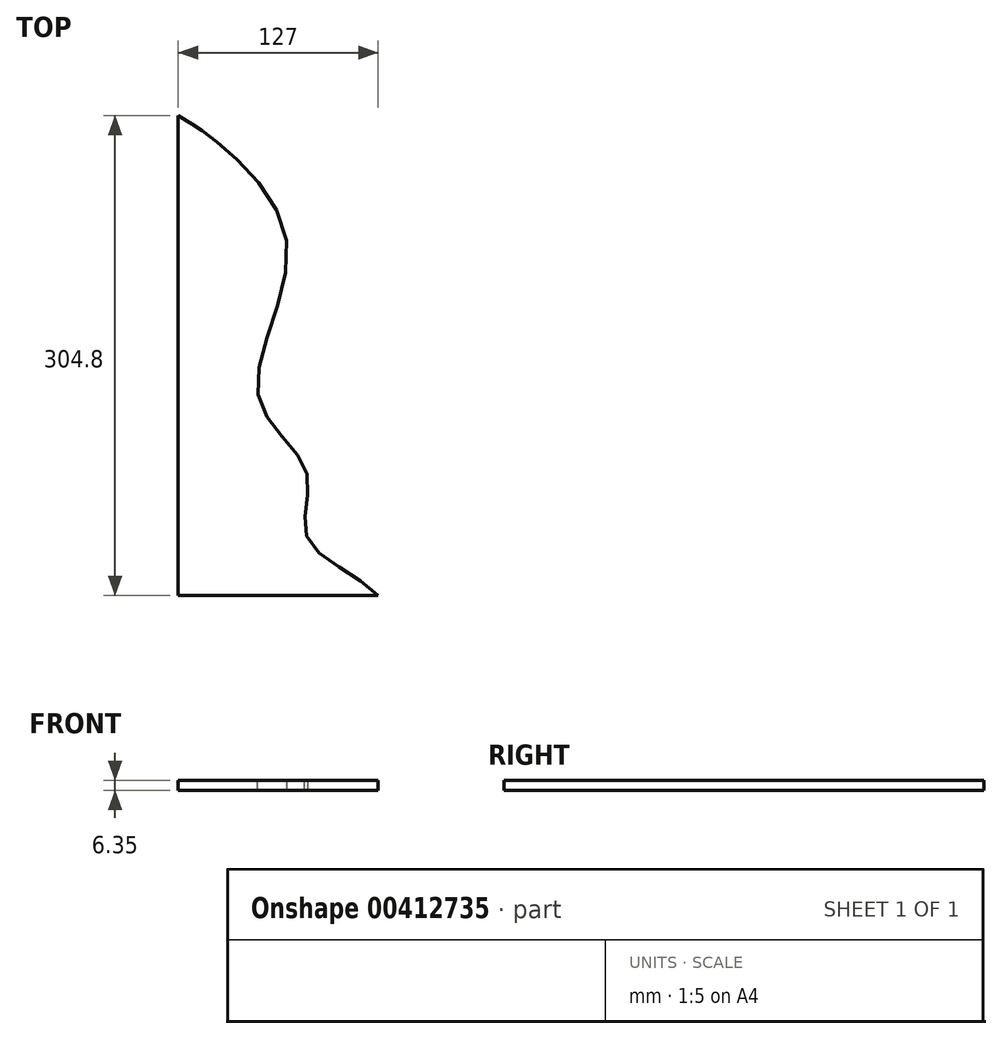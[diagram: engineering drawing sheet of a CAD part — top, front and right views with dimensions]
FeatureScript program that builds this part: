
annotation { "Feature Type Name" : "Feature", "Feature Type Description" : "" }
export const myFeature = defineFeature(function(context is Context, id is Id, definition is map)
    precondition{}
    {
        {
            var Q0;
            Q0=qCreatedBy(makeId("Top.planeOp"),FACE);
            var sketch = newSketch(context, id + "F0", { "sketchPlane" : qUnion([Q0])});
            skLineSegment(sketch, "E0", {"start": v(0, 0) * mm, "end": v(127, 0) * mm});
            skLineSegment(sketch, "E1", {"start": v(0, 0) * mm, "end": v(0, 304.8) * mm});
            skLineSegment(sketch, "E2", {"start": v(0, 127) * mm, "end": v(50.8, 127) * mm, "construction": true});
            skLineSegment(sketch, "E3", {"start": v(0, 293.37) * mm, "end": v(17.78, 293.37) * mm, "construction": true});
            skLineSegment(sketch, "E4", {"start": v(0, 226.06) * mm, "end": v(68.58, 226.06) * mm, "construction": true});
            skLineSegment(sketch, "E5", {"start": v(0, 78.74) * mm, "end": v(81.28, 78.74) * mm, "construction": true});
            skLineSegment(sketch, "E6", {"start": v(0, 60.96) * mm, "end": v(68.58, 60.96) * mm, "construction": true});
            skLineSegment(sketch, "E7", {"start": v(0, 35.56) * mm, "end": v(82.55, 35.56) * mm, "construction": true});
            skFitSpline(sketch, "E8", {"points": [v(0, 304.8) * mm, v(17.78, 293.37) * mm, v(68.58, 226.06) * mm, v(50.8, 127) * mm, v(81.28, 78.74) * mm, v(82.55, 35.56) * mm, v(127, 0) * mm], "startDerivative": vector(278.82, -171.6) * mm, "endDerivative": vector(191.91, -229.02) * mm});
            skSolve(sketch);
        }
        {
            var Q0;
            Q0=makeQuery(id+"F0.imprint","IMPRINT",FACE,{"disambiguationData":[TD([[makeQuery(id+"F0.imprint","IMPRINT",EDGE,{"derivedFrom":sQuery(id+"F0.wireOp",EDGE,"E0")}),1.0]])]});
            extrude(context, id + "F1", {"entities" : qUnion([Q0]), "depth" : 6.35 * mm});
        }
    });
